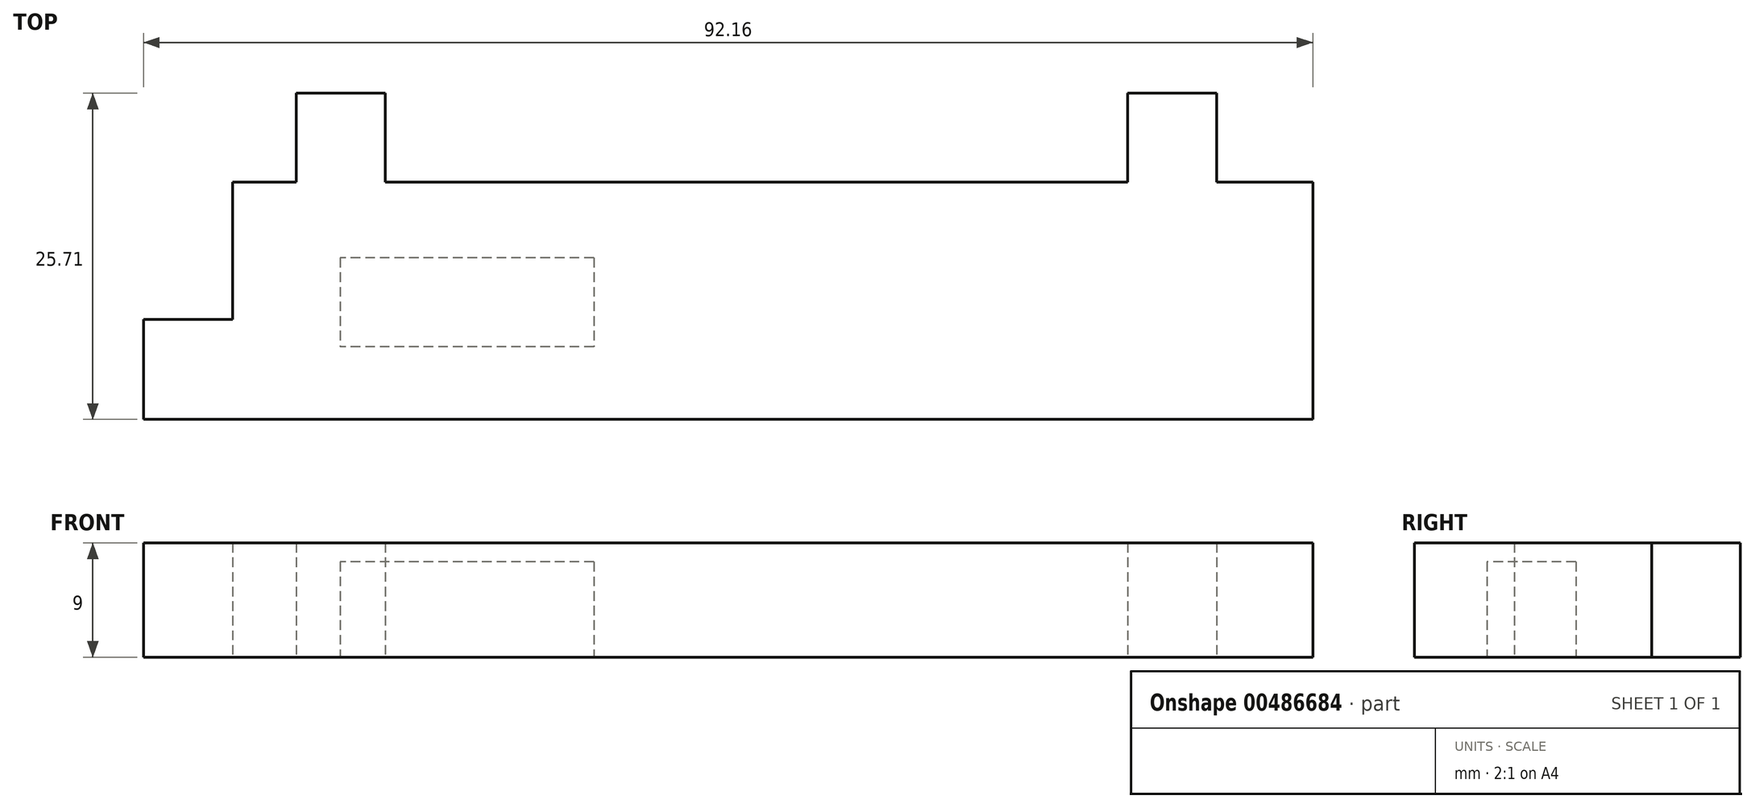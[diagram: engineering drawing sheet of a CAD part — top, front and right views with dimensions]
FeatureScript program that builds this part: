
annotation { "Feature Type Name" : "Feature", "Feature Type Description" : "" }
export const myFeature = defineFeature(function(context is Context, id is Id, definition is map)
    precondition{}
    {
        {
            var Q0;
            Q0=qCreatedBy(makeId("Top.planeOp"),FACE);
            var sketch = newSketch(context, id + "F0", { "sketchPlane" : qUnion([Q0])});
            skLineSegment(sketch, "E0.bottom", {"start": v(-39.38, 0) * mm, "end": v(45.78, 0) * mm});
            skLineSegment(sketch, "E0.top", {"start": v(-39.38, 18.7) * mm, "end": v(45.78, 18.7) * mm});
            skLineSegment(sketch, "E0.left", {"start": v(-39.38, 0) * mm, "end": v(-39.38, 18.7) * mm});
            skLineSegment(sketch, "E0.right", {"start": v(45.78, 0) * mm, "end": v(45.78, 18.7) * mm});
            skLineSegment(sketch, "E1.bottom", {"start": v(-34.34, 18.7) * mm, "end": v(-27.34, 18.7) * mm});
            skLineSegment(sketch, "E1.top", {"start": v(-34.34, 25.7) * mm, "end": v(-27.34, 25.7) * mm});
            skLineSegment(sketch, "E1.left", {"start": v(-34.34, 18.7) * mm, "end": v(-34.34, 25.7) * mm});
            skLineSegment(sketch, "E1.right", {"start": v(-27.34, 18.7) * mm, "end": v(-27.34, 25.7) * mm});
            skLineSegment(sketch, "E2.bottom", {"start": v(31.19, 18.7) * mm, "end": v(38.19, 18.7) * mm});
            skLineSegment(sketch, "E2.top", {"start": v(31.19, 25.7) * mm, "end": v(38.19, 25.7) * mm});
            skLineSegment(sketch, "E2.left", {"start": v(31.19, 18.7) * mm, "end": v(31.19, 25.7) * mm});
            skLineSegment(sketch, "E2.right", {"start": v(38.19, 18.7) * mm, "end": v(38.19, 25.7) * mm});
            skLineSegment(sketch, "E3.bottom", {"start": v(-39.38, 7.88) * mm, "end": v(-46.38, 7.88) * mm});
            skLineSegment(sketch, "E3.top", {"start": v(-39.38, 0) * mm, "end": v(-46.38, 0) * mm});
            skLineSegment(sketch, "E3.left", {"start": v(-39.38, 7.88) * mm, "end": v(-39.38, 0) * mm});
            skLineSegment(sketch, "E3.right", {"start": v(-46.38, 7.88) * mm, "end": v(-46.38, 0) * mm});
            skLineSegment(sketch, "E4.bottom", {"start": v(-10.9, 12.73) * mm, "end": v(-30.9, 12.73) * mm});
            skLineSegment(sketch, "E4.top", {"start": v(-10.9, 5.73) * mm, "end": v(-30.9, 5.73) * mm});
            skLineSegment(sketch, "E4.left", {"start": v(-10.9, 12.73) * mm, "end": v(-10.9, 5.73) * mm});
            skLineSegment(sketch, "E4.right", {"start": v(-30.9, 12.73) * mm, "end": v(-30.9, 5.73) * mm});
            skPoint(sketch, "E4.middle", {"position": v(-20.9, 9.23) * mm});
            skSolve(sketch);
        }
        {
            var Q0;
            Q0 = qSketchRegion(id + "F0", true);
            var Q1;
            Q1=makeQuery(id+"F0.imprint","IMPRINT",FACE,{"disambiguationData":[TD([[makeQuery(id+"F0.imprint","IMPRINT",EDGE,{"derivedFrom":sQuery(id+"F0.wireOp",EDGE,"E4.bottom")}),1.0]])]});
            extrude(context, id + "F1", {"entities" : qUnion([Q0, Q1]), "depth" : 9 * mm});
        }
        {
            var Q0;
            Q0=makeQuery(id+"F0.imprint","IMPRINT",FACE,{"disambiguationData":[TD([[makeQuery(id+"F0.imprint","IMPRINT",EDGE,{"derivedFrom":sQuery(id+"F0.wireOp",EDGE,"E4.bottom")}),1.0]])]});
            extrude(context, id + "F2", {"entities" : qUnion([Q0]), "operationType" : NewBodyOperationType.REMOVE, "oppositeDirection" : true, "depth" : -7.5 * mm});
        }
    });
